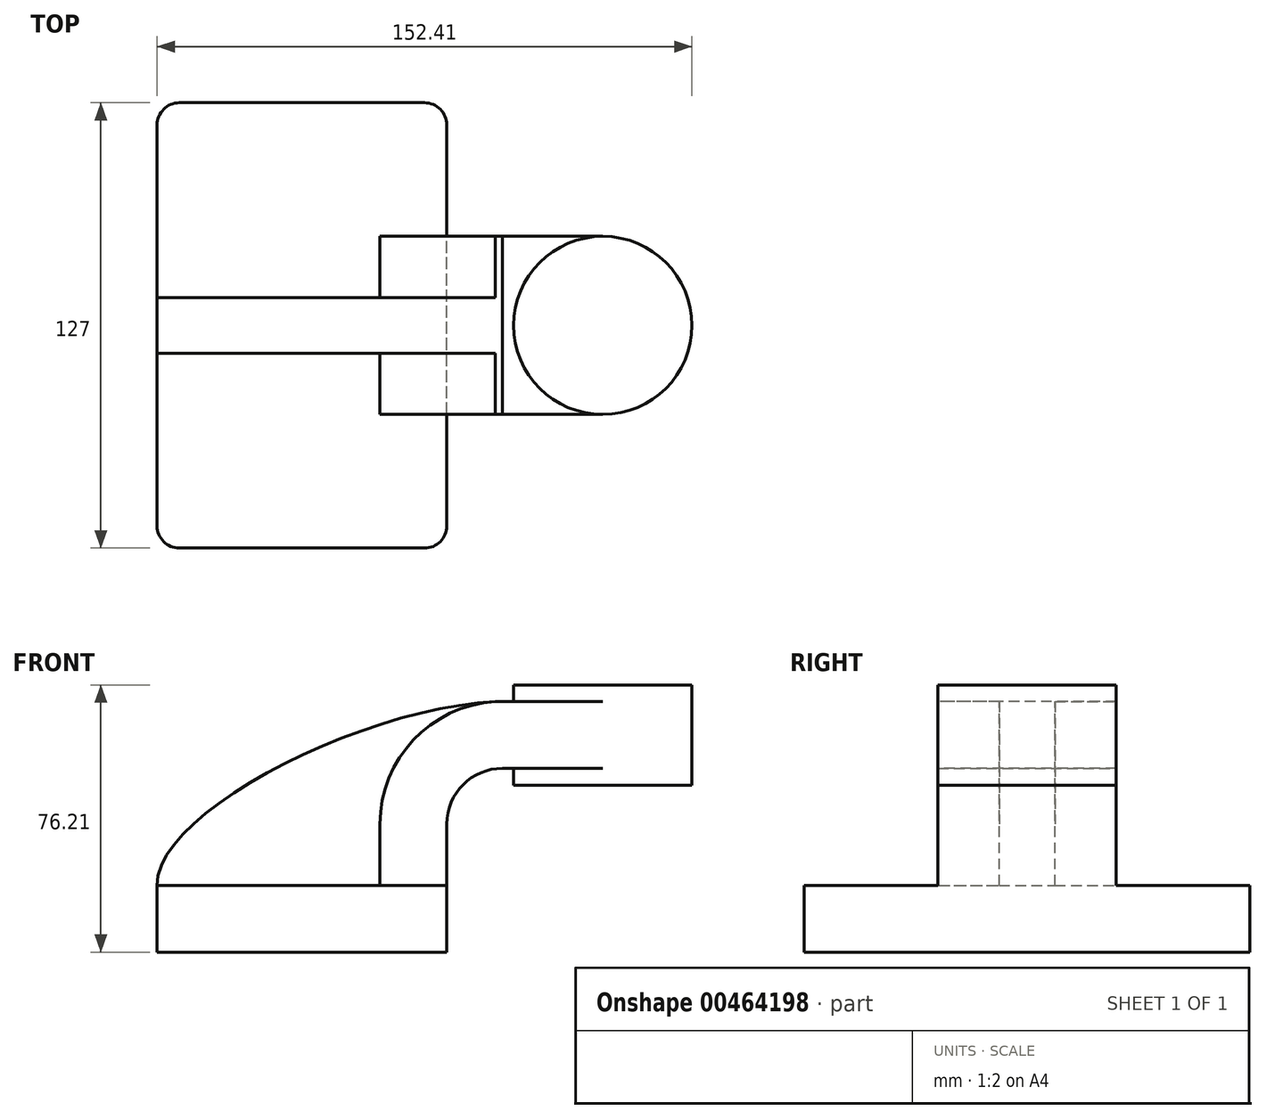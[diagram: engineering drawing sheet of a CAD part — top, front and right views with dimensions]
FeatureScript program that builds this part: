
annotation { "Feature Type Name" : "Feature", "Feature Type Description" : "" }
export const myFeature = defineFeature(function(context is Context, id is Id, definition is map)
    precondition{}
    {
        {
            var Q0;
            Q0=qCreatedBy(makeId("Front.planeOp"),FACE);
            var sketch = newSketch(context, id + "F0", { "sketchPlane" : qUnion([Q0])});
            skLineSegment(sketch, "E0.bottom", {"start": v(-41.28, -9.53) * mm, "end": v(41.28, -9.53) * mm});
            skLineSegment(sketch, "E0.top", {"start": v(-41.28, 9.53) * mm, "end": v(41.28, 9.53) * mm});
            skLineSegment(sketch, "E0.left", {"start": v(-41.28, -9.53) * mm, "end": v(-41.28, 9.53) * mm});
            skLineSegment(sketch, "E0.right", {"start": v(41.28, -9.53) * mm, "end": v(41.28, 9.53) * mm});
            skPoint(sketch, "E0.middle", {"position": v(0, 0) * mm});
            skLineSegment(sketch, "E1.bottom", {"start": v(60.33, 38.1) * mm, "end": v(111.12, 38.1) * mm});
            skLineSegment(sketch, "E1.top", {"start": v(60.32, 66.67) * mm, "end": v(111.12, 66.67) * mm});
            skLineSegment(sketch, "E1.left", {"start": v(60.33, 38.1) * mm, "end": v(60.32, 66.67) * mm});
            skLineSegment(sketch, "E1.right", {"start": v(111.13, 38.1) * mm, "end": v(111.12, 66.67) * mm});
            skPoint(sketch, "E1.middle", {"position": v(85.72, 52.39) * mm});
            skLineSegment(sketch, "E2", {"start": v(41.27, 9.53) * mm, "end": v(41.27, 27) * mm});
            skArc(sketch, "E3", {"start": v(41.27, 27) * mm, "mid": v(45.92, 38.23) * mm, "end": v(57.15, 42.88) * mm});
            skLineSegment(sketch, "E4", {"start": v(57.15, 42.88) * mm, "end": v(85.72, 42.88) * mm});
            skLineSegment(sketch, "E5.0", {"start": v(57.15, 61.93) * mm, "end": v(85.72, 61.93) * mm});
            skArc(sketch, "E5.1", {"start": v(22.22, 27) * mm, "mid": v(32.45, 51.7) * mm, "end": v(57.15, 61.93) * mm});
            skLineSegment(sketch, "E5.2", {"start": v(22.22, 9.53) * mm, "end": v(22.22, 27) * mm});
            skLineSegment(sketch, "E6", {"start": v(85.73, 38.1) * mm, "end": v(85.73, 42.88) * mm});
            skLineSegment(sketch, "E7", {"start": v(85.73, 52.39) * mm, "end": v(85.72, 61.93) * mm});
            skLineSegment(sketch, "E8", {"start": v(85.72, 61.93) * mm, "end": v(85.72, 66.67) * mm});
            skFitSpline(sketch, "E9", {"points": [v(-41.28, 9.53) * mm, v(57.15, 61.93) * mm], "startDerivative": vector(-1.29, 63.94) * mm, "endDerivative": vector(113.33, 1.78) * mm});
            skLineSegment(sketch, "E10", {"start": v(85.72, 52.39) * mm, "end": v(85.72, 42.88) * mm});
            skSolve(sketch);
        }
        {
            var Q0;
            Q0=makeQuery(id+"F0.imprint","IMPRINT",FACE,{"disambiguationData":[TD([[makeQuery(id+"F0.imprint","IMPRINT",EDGE,{"derivedFrom":sQuery(id+"F0.wireOp",EDGE,"E0.bottom")}),1.0]])]});
            extrude(context, id + "F1", {"entities" : qUnion([Q0]), "endBound" : BoundingType.SYMMETRIC, "depth" : 127 * mm});
        }
        {
            var Q0;
            {var subQ0=sQuery(id+"F0.wireOp",EDGE,"E7");Q0=makeQuery(id+"F0.imprint","IMPRINT",FACE,{"disambiguationData":[TD([[makeQuery(id+"F0.imprint","IMPRINT",EDGE,{"derivedFrom":subQ0}),1.0]])]});}
            var Q1;
            {var subQ1=sQuery(id+"F0.wireOp",EDGE,"E2");Q1=makeQuery(id+"F0.imprint","IMPRINT",FACE,{"disambiguationData":[TD([[makeQuery(id+"F0.imprint","IMPRINT",EDGE,{"derivedFrom":subQ1}),1.0]])]});}
            extrude(context, id + "F2", {"entities" : qUnion([Q0, Q1]), "operationType" : NewBodyOperationType.ADD, "endBound" : BoundingType.SYMMETRIC, "depth" : 50.8 * mm});
        }
        {
            var Q0;
            {var subQ3=sQuery(id+"F0.wireOp",EDGE,"E5.2");Q0=makeQuery(id+"F0.imprint","IMPRINT",FACE,{"disambiguationData":[TD([[makeQuery(id+"F0.imprint","IMPRINT",EDGE,{"derivedFrom":subQ3}),1.0]])]});}
            extrude(context, id + "F3", {"entities" : qUnion([Q0]), "operationType" : NewBodyOperationType.ADD, "endBound" : BoundingType.SYMMETRIC, "depth" : 15.88 * mm});
        }
        {
            var Q0;
            {var subQ1=sQuery(id+"F0.wireOp",EDGE,"E1.right");Q0=makeQuery(id+"F0.imprint","IMPRINT",FACE,{"disambiguationData":[TD([[makeQuery(id+"F0.imprint","IMPRINT",EDGE,{"derivedFrom":subQ1}),1.0]])]});}
            var Q1;
            Q1=sQuery(id+"F0.wireOp",EDGE,"E10");
            revolve(context, id + "F4", {"operationType" : NewBodyOperationType.ADD, "entities" : qUnion([Q0]), "axis" : qUnion([Q1]), "revolveType" : RevolveType.FULL});
        }
        {
            var Q0;
            Q0=makeQuery(id+"F1.opExtrude","CAP_EDGE",EDGE,{"disambiguationData":[OSD([sQuery(id+"F0.wireOp",EDGE,"E0.left")])],"isStart":false});
            var Q1;
            Q1=makeQuery(id+"F1.opExtrude","CAP_EDGE",EDGE,{"disambiguationData":[OSD([sQuery(id+"F0.wireOp",EDGE,"E0.right")])],"isStart":true});
            var Q2;
            Q2=makeQuery(id+"F1.opExtrude","CAP_EDGE",EDGE,{"disambiguationData":[OSD([sQuery(id+"F0.wireOp",EDGE,"E0.right")])],"isStart":false});
            var Q3;
            Q3=makeQuery(id+"F1.opExtrude","CAP_EDGE",EDGE,{"disambiguationData":[OSD([sQuery(id+"F0.wireOp",EDGE,"E0.left")])],"isStart":true});
            fillet(context, id + "F5", {"entities" : qUnion([Q0, Q1, Q2, Q3]), "radius" : 6.35 * mm, "tangentPropagation" : true, "allowEdgeOverflow" : false});
        }
    });
